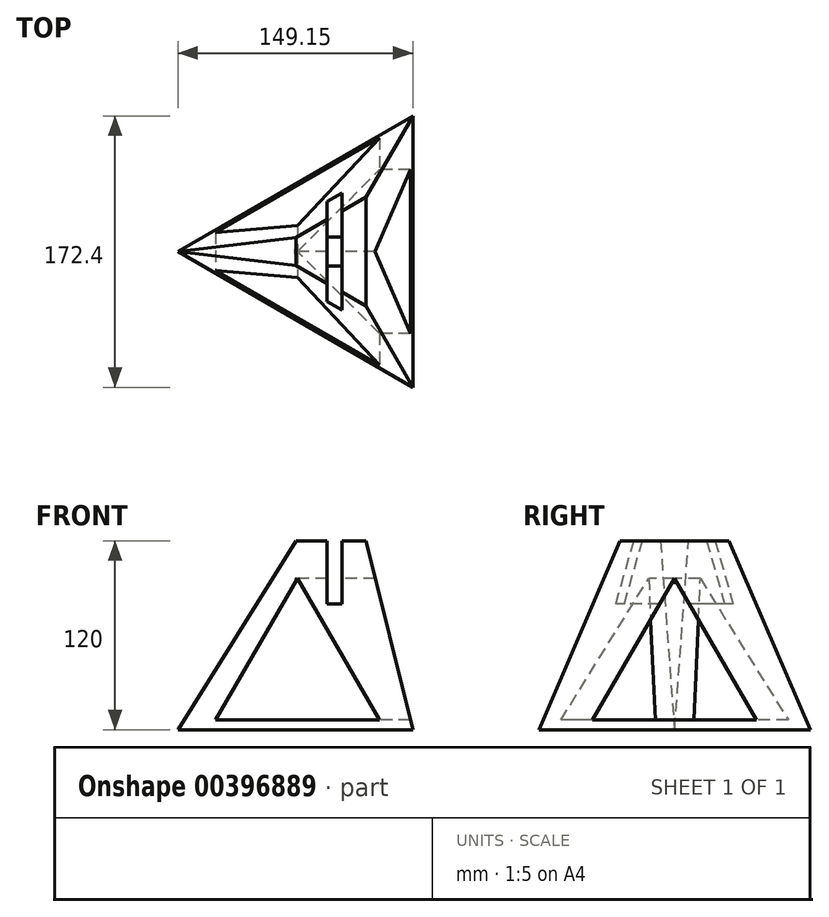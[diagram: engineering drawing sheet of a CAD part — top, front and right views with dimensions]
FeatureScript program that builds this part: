
annotation { "Feature Type Name" : "Feature", "Feature Type Description" : "" }
export const myFeature = defineFeature(function(context is Context, id is Id, definition is map)
    precondition{}
    {
        {
            var Q0;
            Q0=qCreatedBy(makeId("Top.planeOp"),FACE);
            var sketch = newSketch(context, id + "F0", { "sketchPlane" : qUnion([Q0])});
            skCircle(sketch, "E0.cCircle", {"center": v(0, 0) * mm, "radius": 49.77 * mm, "construction": true});
            skLineSegment(sketch, "E0.0", {"start": v(49.77, 86.2) * mm, "end": v(49.77, -86.2) * mm});
            skLineSegment(sketch, "E0.1", {"start": v(49.77, -86.2) * mm, "end": v(-99.54, 0) * mm});
            skLineSegment(sketch, "E0.2", {"start": v(-99.54, 0) * mm, "end": v(49.77, 86.2) * mm});
            skPoint(sketch, "E0.0.midPoint", {"position": v(49.77, 0) * mm});
            skSolve(sketch);
        }
        {
            var Q0;
            Q0=qCreatedBy(makeId("Top.planeOp"),FACE);
            cPlane(context, id + "F1", {"entities" : qUnion([Q0]), "cplaneType" : CPlaneType.OFFSET, "offset" : 120 * mm, "width" : 150 * mm, "height" : 150 * mm});
        }
        {
            var Q0;
            Q0=qCreatedBy(id+"F1.planeOp",FACE);
            var sketch = newSketch(context, id + "F2", { "sketchPlane" : qUnion([Q0])});
            skCircle(sketch, "E1.cCircle", {"center": v(0, 0) * mm, "radius": 19.95 * mm, "construction": true});
            skLineSegment(sketch, "E1.0", {"start": v(19.95, 34.56) * mm, "end": v(19.95, -34.56) * mm});
            skLineSegment(sketch, "E1.1", {"start": v(19.95, -34.56) * mm, "end": v(-39.9, 0) * mm});
            skLineSegment(sketch, "E1.2", {"start": v(-39.9, 0) * mm, "end": v(19.95, 34.56) * mm});
            skPoint(sketch, "E1.0.midPoint", {"position": v(19.95, 0) * mm});
            skSolve(sketch);
        }
        {
            var Q0;
            Q0=makeQuery(id+"F0.imprint","IMPRINT",FACE,{"disambiguationData":[TD([[makeQuery(id+"F0.imprint","IMPRINT",EDGE,{"derivedFrom":sQuery(id+"F0.wireOp",EDGE,"E0.0")}),-1.0]])]});
            var Q1;
            Q1=makeQuery(id+"F2.imprint","IMPRINT",FACE,{"disambiguationData":[TD([[makeQuery(id+"F2.imprint","IMPRINT",EDGE,{"derivedFrom":sQuery(id+"F2.wireOp",EDGE,"E1.0")}),-1.0]])]});
            loft(context, id + "F3", {"sheetProfilesArray" : [{ "sheetProfileEntities" : qUnion([Q0]) }, { "sheetProfileEntities" : qUnion([Q1]) }]});
        }
        {
            var Q0;
            Q0=makeQuery(id+"F3.opLoft","CAP_FACE",FACE,{"disambiguationData":[OSD([makeQuery(id+"F2.imprint","IMPRINT",FACE,{"disambiguationData":[TD([[makeQuery(id+"F2.imprint","IMPRINT",EDGE,{"derivedFrom":sQuery(id+"F2.wireOp",EDGE,"E1.0")}),-1.0]])]})])],"isStart":true});
            var sketch = newSketch(context, id + "F4", { "sketchPlane" : qUnion([Q0])});
            skLineSegment(sketch, "E2.bottom", {"start": v(4.7, 48.16) * mm, "end": v(-4.7, 48.16) * mm});
            skLineSegment(sketch, "E2.top", {"start": v(4.7, -48.16) * mm, "end": v(-4.7, -48.16) * mm});
            skLineSegment(sketch, "E2.left", {"start": v(4.7, 48.16) * mm, "end": v(4.7, -48.16) * mm});
            skLineSegment(sketch, "E2.right", {"start": v(-4.7, 48.16) * mm, "end": v(-4.7, -48.16) * mm});
            skPoint(sketch, "E2.middle", {"position": v(0, 0) * mm});
            skSolve(sketch);
        }
        {
            var Q0;
            {var subQ0=sQuery(id+"F4.wireOp",EDGE,"E2.left");var subQ1=sQuery(id+"F2.wireOp",EDGE,"E1.2");var subQ2=sQuery(id+"F2.wireOp",EDGE,"E1.1");var subQ3=makeQuery(id+"F2.imprint","INTERSECT",VERTEX,{"derivedFrom":[subQ2,subQ1]});var subQ4=sQuery(id+"F2.wireOp",EDGE,"E1.0");var subQ5=makeQuery(id+"F3.opLoft","MID_CAP_EDGE",EDGE,{"disambiguationData":[OSD([subQ4,subQ2,subQ1]),TDD([makeQuery(id+"F2.imprint","INTERSECT",VERTEX,{"derivedFrom":[subQ4,subQ1]}),subQ3,makeQuery(id+"F2.imprint","IMPRINT",EDGE,{"derivedFrom":subQ1})])],"capPos":1.0});var subQ6=makeQuery(id+"F4.imprint","INTERSECT",VERTEX,{"derivedFrom":[subQ5,subQ0]});Q0=makeQuery(id+"F4.imprint","IMPRINT",FACE,{"disambiguationData":[TD([[makeQuery(id+"F4.imprint","IMPRINT",EDGE,{"disambiguationData":[TD([[subQ6,-1.0]])],"derivedFrom":subQ0}),-1.0]])]});}
            var Q1;
            {var subQ0=sQuery(id+"F4.wireOp",EDGE,"E2.bottom");Q1=makeQuery(id+"F4.imprint","IMPRINT",FACE,{"disambiguationData":[TD([[makeQuery(id+"F4.imprint","IMPRINT",EDGE,{"derivedFrom":subQ0}),1.0]])]});}
            var Q2;
            {var subQ0=sQuery(id+"F4.wireOp",EDGE,"E2.top");Q2=makeQuery(id+"F4.imprint","IMPRINT",FACE,{"disambiguationData":[TD([[makeQuery(id+"F4.imprint","IMPRINT",EDGE,{"derivedFrom":subQ0}),-1.0]])]});}
            extrude(context, id + "F5", {"entities" : qUnion([Q0, Q1, Q2]), "operationType" : NewBodyOperationType.REMOVE, "oppositeDirection" : true, "depth" : 40 * mm});
        }
        {
            var Q0;
            {var subQ4=sQuery(id+"F2.wireOp",EDGE,"E1.0");Q0=makeQuery(id+"F5.boolean.opBoolean","SPLIT",FACE,{"disambiguationData":[TD([makeQuery(id+"F5.opExtrude","SWEPT_FACE",FACE,{"disambiguationData":[OSD([sQuery(id+"F4.wireOp",EDGE,"E2.right")])]})])],"derivedFrom":makeQuery(id+"F3.opLoft","CAP_FACE",FACE,{"disambiguationData":[OSD([makeQuery(id+"F2.imprint","IMPRINT",FACE,{"disambiguationData":[TD([[makeQuery(id+"F2.imprint","IMPRINT",EDGE,{"derivedFrom":subQ4}),-1.0]])]})])],"isStart":true})});}
            var sketch = newSketch(context, id + "F6", { "sketchPlane" : qUnion([Q0])});
            skLineSegment(sketch, "E3.bottom", {"start": v(-40.4, -19.67) * mm, "end": v(-24.4, -19.67) * mm});
            skLineSegment(sketch, "E3.top", {"start": v(-40.4, 19.67) * mm, "end": v(-24.4, 19.67) * mm});
            skLineSegment(sketch, "E3.left", {"start": v(-40.4, -19.67) * mm, "end": v(-40.4, 19.67) * mm});
            skLineSegment(sketch, "E3.right", {"start": v(-24.4, -19.67) * mm, "end": v(-24.4, 19.67) * mm});
            skPoint(sketch, "E3.middle", {"position": v(-32.4, 0) * mm});
            skSolve(sketch);
        }
        {
            var Q0;
            Q0=qCreatedBy(makeId("Front.planeOp"),FACE);
            var sketch = newSketch(context, id + "F7", { "sketchPlane" : qUnion([Q0])});
            skLineSegment(sketch, "E4", {"start": v(-31.97, 120.5) * mm, "end": v(-107.25, 0) * mm});
            skSolve(sketch);
        }
        {
            var Q0;
            {var subQ0=sQuery(id+"F6.wireOp",EDGE,"E3.right");var subQ1=sQuery(id+"F2.wireOp",EDGE,"E1.2");var subQ3=sQuery(id+"F2.wireOp",EDGE,"E1.1");var subQ4=makeQuery(id+"F2.imprint","INTERSECT",VERTEX,{"derivedFrom":[subQ3,subQ1]});var subQ5=sQuery(id+"F2.wireOp",EDGE,"E1.0");var subQ12=makeQuery(id+"F2.imprint","IMPRINT",EDGE,{"derivedFrom":subQ3});var subQ13=makeQuery(id+"F2.imprint","INTERSECT",VERTEX,{"derivedFrom":[subQ5,subQ3]});var subQ16=makeQuery(id+"F5.opExtrude","SWEPT_FACE",FACE,{"disambiguationData":[OSD([sQuery(id+"F4.wireOp",EDGE,"E2.right")])]});var subQ17=makeQuery(id+"F5.boolean.opBoolean","SPLIT",EDGE,{"disambiguationData":[TD([subQ16])],"derivedFrom":makeQuery(id+"F3.opLoft","MID_CAP_EDGE",EDGE,{"disambiguationData":[OSD([subQ5,subQ3,subQ1]),TDD([subQ13,subQ4,subQ12])],"capPos":1.0})});var subQ18=makeQuery(id+"F6.imprint","INTERSECT",VERTEX,{"derivedFrom":[subQ17,subQ0]});Q0=makeQuery(id+"F6.imprint","IMPRINT",FACE,{"disambiguationData":[TD([[makeQuery(id+"F6.imprint","IMPRINT",EDGE,{"disambiguationData":[TD([[subQ18,-1.0]])],"derivedFrom":subQ0}),1.0]])]});}
            var Q1;
            Q1=sQuery(id+"F7.wireOp",EDGE,"E4");
            sweep(context, id + "F8", {"operationType" : NewBodyOperationType.REMOVE, "profiles" : qUnion([Q0]), "path" : qUnion([Q1])});
        }
        {
            var Q0;
            Q0=qCreatedBy(makeId("Front.planeOp"),FACE);
            var sketch = newSketch(context, id + "F9", { "sketchPlane" : qUnion([Q0])});
            skCircle(sketch, "E5.cCircle", {"center": v(-23.43, 36.1) * mm, "radius": 30 * mm, "construction": true});
            skLineSegment(sketch, "E5.0", {"start": v(28.53, 6.1) * mm, "end": v(-75.4, 6.1) * mm});
            skLineSegment(sketch, "E5.1", {"start": v(-75.4, 6.1) * mm, "end": v(-23.43, 96.1) * mm});
            skLineSegment(sketch, "E5.2", {"start": v(-23.43, 96.1) * mm, "end": v(28.53, 6.1) * mm});
            skPoint(sketch, "E5.0.midPoint", {"position": v(-23.43, 6.1) * mm});
            skSolve(sketch);
        }
        {
            var Q0;
            Q0 = qSketchRegion(id + "F9", true);
            extrude(context, id + "F10", {"entities" : qUnion([Q0]), "operationType" : NewBodyOperationType.REMOVE, "oppositeDirection" : true, "depth" : 100 * mm, "hasSecondDirection" : true, "secondDirectionOppositeDirection" : false, "secondDirectionDepth" : 100 * mm});
        }
        {
            var Q0;
            Q0=qCreatedBy(makeId("Right.planeOp"),FACE);
            var sketch = newSketch(context, id + "F11", { "sketchPlane" : qUnion([Q0])});
            skCircle(sketch, "E6.cCircle", {"center": v(0, 36.1) * mm, "radius": 30 * mm, "construction": true});
            skLineSegment(sketch, "E6.0", {"start": v(51.96, 6.1) * mm, "end": v(-51.96, 6.1) * mm});
            skLineSegment(sketch, "E6.1", {"start": v(-51.96, 6.1) * mm, "end": v(0, 96.1) * mm});
            skLineSegment(sketch, "E6.2", {"start": v(0, 96.1) * mm, "end": v(51.96, 6.1) * mm});
            skPoint(sketch, "E6.0.midPoint", {"position": v(0, 6.1) * mm});
            skLineSegment(sketch, "E7.0.0", {"start": v(-34.56, 120) * mm, "end": v(34.56, 120) * mm, "construction": true});
            skLineSegment(sketch, "E7.0.1", {"start": v(-34.56, 120) * mm, "end": v(-86.2, 0) * mm, "construction": true});
            skLineSegment(sketch, "E7.0.2", {"start": v(-86.2, 0) * mm, "end": v(86.2, 0) * mm, "construction": true});
            skLineSegment(sketch, "E7.0.3", {"start": v(86.2, 0) * mm, "end": v(34.56, 120) * mm, "construction": true});
            skSolve(sketch);
        }
        {
            var Q0;
            Q0=makeQuery(id+"F11.imprint","IMPRINT",FACE,{"disambiguationData":[TD([[makeQuery(id+"F11.imprint","IMPRINT",EDGE,{"derivedFrom":sQuery(id+"F11.wireOp",EDGE,"E6.0")}),-1.0]])]});
            extrude(context, id + "F12", {"entities" : qUnion([Q0]), "operationType" : NewBodyOperationType.REMOVE, "depth" : 100 * mm, "hasSecondDirection" : true, "secondDirectionOppositeDirection" : true, "secondDirectionDepth" : 25 * mm});
        }
    });
